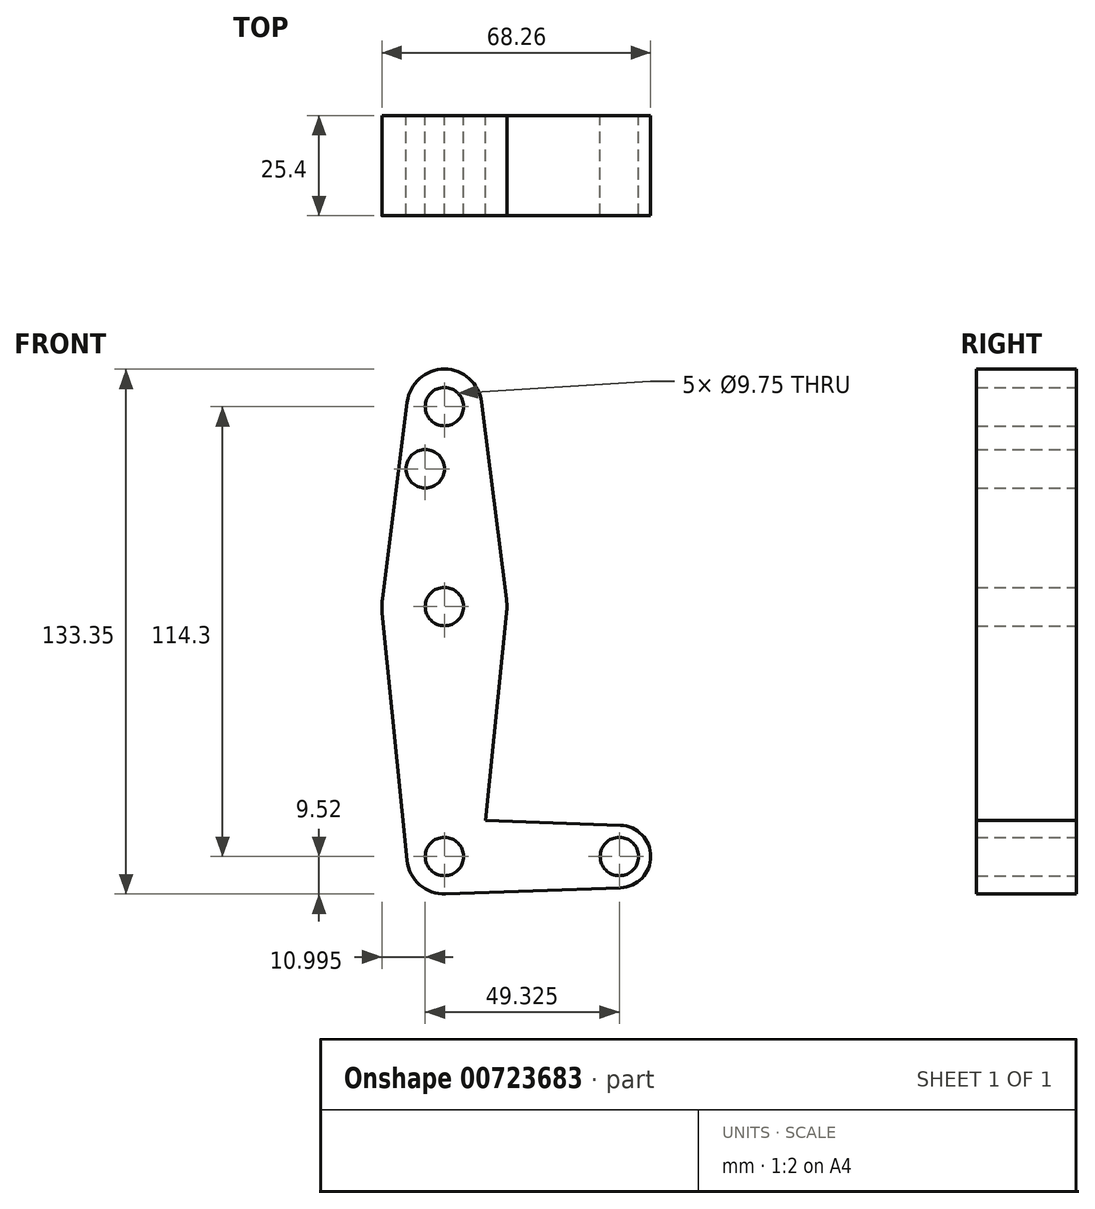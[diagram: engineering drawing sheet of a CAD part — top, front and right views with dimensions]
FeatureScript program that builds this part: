
annotation { "Feature Type Name" : "Feature", "Feature Type Description" : "" }
export const myFeature = defineFeature(function(context is Context, id is Id, definition is map)
    precondition{}
    {
        {
            var Q0;
            Q0=qCreatedBy(makeId("Front.planeOp"),FACE);
            var sketch = newSketch(context, id + "F0", { "sketchPlane" : qUnion([Q0])});
            skLineSegment(sketch, "E0", {"start": v(0, 0) * mm, "end": v(44.45, 0) * mm, "construction": true});
            skLineSegment(sketch, "E1", {"start": v(0, 0) * mm, "end": v(0, 114.3) * mm, "construction": true});
            skCircle(sketch, "E2", {"center": v(0, 114.3) * mm, "radius": 9.53 * mm});
            skCircle(sketch, "E3", {"center": v(0, 0) * mm, "radius": 9.53 * mm});
            skCircle(sketch, "E4", {"center": v(44.45, 0) * mm, "radius": 7.94 * mm});
            skCircle(sketch, "E5", {"center": v(0, 63.5) * mm, "radius": 15.88 * mm});
            skLineSegment(sketch, "E6", {"start": v(9.45, 115.5) * mm, "end": v(15.75, 65.48) * mm});
            skLineSegment(sketch, "E7", {"start": v(-9.45, 115.5) * mm, "end": v(-15.75, 65.48) * mm});
            skLineSegment(sketch, "E8", {"start": v(-15.8, 61.91) * mm, "end": v(-9.48, -0.95) * mm});
            skLineSegment(sketch, "E9", {"start": v(15.8, 61.91) * mm, "end": v(9.48, -0.95) * mm});
            skLineSegment(sketch, "E10", {"start": v(0.34, -9.52) * mm, "end": v(44.73, -7.93) * mm});
            skLineSegment(sketch, "E11", {"start": v(0.34, 9.52) * mm, "end": v(44.73, 7.93) * mm});
            skCircle(sketch, "E12", {"center": v(0, 114.3) * mm, "radius": 4.87 * mm});
            skCircle(sketch, "E13", {"center": v(0, 63.5) * mm, "radius": 4.87 * mm});
            skCircle(sketch, "E14", {"center": v(0, 0) * mm, "radius": 4.87 * mm});
            skCircle(sketch, "E15", {"center": v(44.45, 0) * mm, "radius": 4.87 * mm});
            skCircle(sketch, "E16", {"center": v(-4.87, 98.5) * mm, "radius": 4.87 * mm});
            skSolve(sketch);
        }
        {
            var Q0;
            Q0 = qSketchRegion(id + "F0", true);
            extrude(context, id + "F1", {"entities" : qUnion([Q0]), "depth" : 25.4 * mm, "offsetDistance" : 25.4 * mm});
        }
    });
